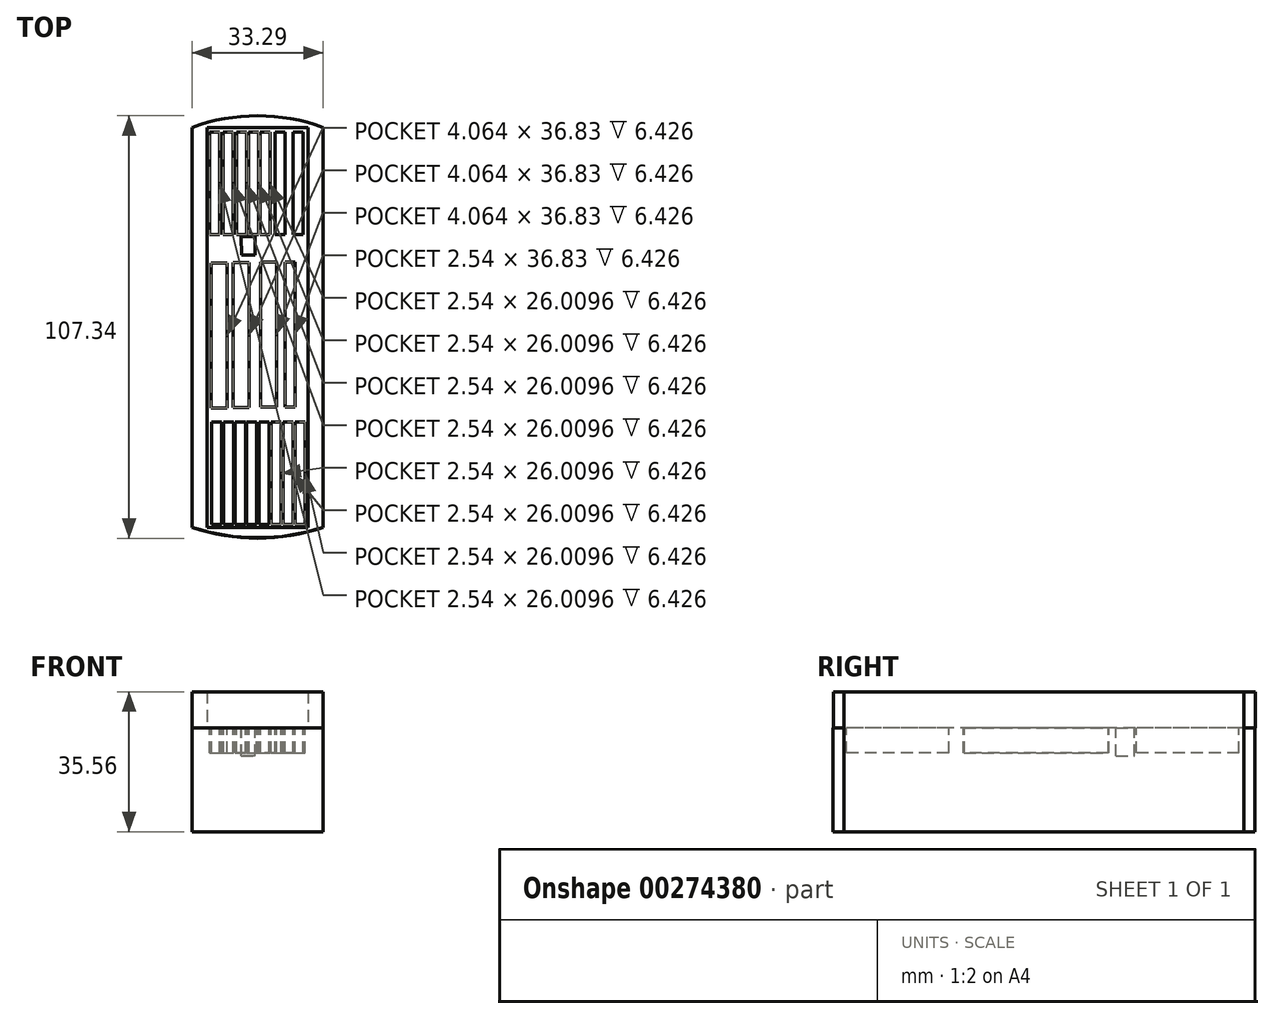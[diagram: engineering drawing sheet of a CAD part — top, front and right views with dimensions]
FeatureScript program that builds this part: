
annotation { "Feature Type Name" : "Feature", "Feature Type Description" : "" }
export const myFeature = defineFeature(function(context is Context, id is Id, definition is map)
    precondition{}
    {
        {
            var Q0;
            Q0=qCreatedBy(makeId("Top.planeOp"),FACE);
            var sketch = newSketch(context, id + "F0", { "sketchPlane" : qUnion([Q0])});
            skLineSegment(sketch, "E0", {"start": v(11.71, 60.5) * mm, "end": v(11.71, -41.1) * mm});
            skLineSegment(sketch, "E1", {"start": v(45, 60.5) * mm, "end": v(45, -41.1) * mm});
            skArc(sketch, "E2", {"start": v(45, 60.5) * mm, "mid": v(28.36, 63.3) * mm, "end": v(11.71, 60.5) * mm});
            skArc(sketch, "E3", {"start": v(11.71, -41.1) * mm, "mid": v(28.36, -43.9) * mm, "end": v(45, -41.1) * mm});
            skSolve(sketch);
        }
        {
            var Q0;
            Q0 = qSketchRegion(id + "F0", true);
            extrude(context, id + "F1", {"entities" : qUnion([Q0]), "depth" : 26.42 * mm});
        }
        {
            var Q0;
            Q0=makeQuery(id+"F1.opExtrude","CAP_FACE",FACE,{"disambiguationData":[OSD([sQuery(id+"F0.wireOp",EDGE,"E0"),sQuery(id+"F0.wireOp",EDGE,"E1"),sQuery(id+"F0.wireOp",EDGE,"E2"),sQuery(id+"F0.wireOp",EDGE,"E3")])],"isStart":false});
            var sketch = newSketch(context, id + "F2", { "sketchPlane" : qUnion([Q0])});
            skLineSegment(sketch, "E4", {"start": v(24.2, 32.75) * mm, "end": v(27.71, 32.75) * mm});
            skLineSegment(sketch, "E5", {"start": v(27.71, 32.75) * mm, "end": v(27.71, 28.02) * mm});
            skLineSegment(sketch, "E6", {"start": v(27.71, 28.02) * mm, "end": v(24.34, 28.02) * mm});
            skLineSegment(sketch, "E7", {"start": v(24.34, 28.02) * mm, "end": v(24.2, 32.75) * mm});
            skSolve(sketch);
        }
        {
            var Q0;
            Q0 = qSketchRegion(id + "F2", true);
            extrude(context, id + "F3", {"entities" : qUnion([Q0]), "operationType" : NewBodyOperationType.REMOVE, "oppositeDirection" : true, "depth" : 7.2 * mm});
        }
        {
            var Q0;
            Q0=makeQuery(id+"F1.opExtrude","CAP_FACE",FACE,{"disambiguationData":[OSD([sQuery(id+"F0.wireOp",EDGE,"E0"),sQuery(id+"F0.wireOp",EDGE,"E1"),sQuery(id+"F0.wireOp",EDGE,"E2"),sQuery(id+"F0.wireOp",EDGE,"E3")])],"isStart":false});
            var sketch = newSketch(context, id + "F4", { "sketchPlane" : qUnion([Q0])});
            skLineSegment(sketch, "E8", {"start": v(11.71, 60.5) * mm, "end": v(15.48, 60.5) * mm});
            skLineSegment(sketch, "E9", {"start": v(15.48, 60.5) * mm, "end": v(15.48, -41.1) * mm});
            skLineSegment(sketch, "E10", {"start": v(45, 60.5) * mm, "end": v(41.24, 60.5) * mm});
            skLineSegment(sketch, "E11", {"start": v(41.24, 60.5) * mm, "end": v(41.24, -41.1) * mm});
            skLineSegment(sketch, "E12", {"start": v(41.24, -41.1) * mm, "end": v(45, -41.1) * mm});
            skLineSegment(sketch, "E13", {"start": v(45, -41.1) * mm, "end": v(45, 60.5) * mm});
            skLineSegment(sketch, "E14", {"start": v(11.71, 60.5) * mm, "end": v(11.71, -41.1) * mm});
            skLineSegment(sketch, "E15", {"start": v(11.71, -41.1) * mm, "end": v(15.48, -41.1) * mm});
            skSolve(sketch);
        }
        {
            var Q0;
            Q0 = qSketchRegion(id + "F4", true);
            extrude(context, id + "F5", {"entities" : qUnion([Q0]), "operationType" : NewBodyOperationType.ADD, "depth" : 9.14 * mm});
        }
        {
            var Q0;
            Q0=makeQuery(id+"F1.opExtrude","CAP_FACE",FACE,{"disambiguationData":[OSD([sQuery(id+"F0.wireOp",EDGE,"E0"),sQuery(id+"F0.wireOp",EDGE,"E1"),sQuery(id+"F0.wireOp",EDGE,"E2"),sQuery(id+"F0.wireOp",EDGE,"E3")])],"isStart":false});
            var sketch = newSketch(context, id + "F6", { "sketchPlane" : qUnion([Q0])});
            skLineSegment(sketch, "E16.bottom", {"start": v(16.54, 26.06) * mm, "end": v(20.6, 26.06) * mm});
            skLineSegment(sketch, "E16.top", {"start": v(16.54, -10.77) * mm, "end": v(20.6, -10.77) * mm});
            skLineSegment(sketch, "E16.left", {"start": v(16.54, 26.06) * mm, "end": v(16.54, -10.77) * mm});
            skLineSegment(sketch, "E16.right", {"start": v(20.6, 26.06) * mm, "end": v(20.6, -10.77) * mm});
            skPoint(sketch, "E17.oppositeSnap0", {"position": v(30.78, -24.01) * mm});
            skLineSegment(sketch, "E18.bottom", {"start": v(26.22, -10.64) * mm, "end": v(22.15, -10.64) * mm});
            skLineSegment(sketch, "E18.top", {"start": v(26.22, 26.2) * mm, "end": v(22.15, 26.2) * mm});
            skLineSegment(sketch, "E18.left", {"start": v(26.22, -10.64) * mm, "end": v(26.22, 26.2) * mm});
            skLineSegment(sketch, "E18.right", {"start": v(22.15, -10.64) * mm, "end": v(22.15, 26.2) * mm});
            skLineSegment(sketch, "E19.bottom", {"start": v(33.2, -10.54) * mm, "end": v(29.14, -10.54) * mm});
            skLineSegment(sketch, "E19.top", {"start": v(33.2, 26.29) * mm, "end": v(29.14, 26.29) * mm});
            skLineSegment(sketch, "E19.left", {"start": v(33.2, -10.54) * mm, "end": v(33.2, 26.29) * mm});
            skLineSegment(sketch, "E19.right", {"start": v(29.14, -10.54) * mm, "end": v(29.14, 26.29) * mm});
            skLineSegment(sketch, "E20.bottom", {"start": v(37.85, -10.61) * mm, "end": v(35.3, -10.61) * mm});
            skLineSegment(sketch, "E20.top", {"start": v(37.85, 26.22) * mm, "end": v(35.3, 26.22) * mm});
            skLineSegment(sketch, "E20.left", {"start": v(37.85, -10.61) * mm, "end": v(37.85, 26.22) * mm});
            skLineSegment(sketch, "E20.right", {"start": v(35.3, -10.61) * mm, "end": v(35.3, 26.22) * mm});
            skLineSegment(sketch, "E21.bottom", {"start": v(16.67, -40.43) * mm, "end": v(19.21, -40.43) * mm});
            skLineSegment(sketch, "E21.top", {"start": v(16.67, -14.42) * mm, "end": v(19.21, -14.42) * mm});
            skLineSegment(sketch, "E21.left", {"start": v(16.67, -40.43) * mm, "end": v(16.67, -14.42) * mm});
            skLineSegment(sketch, "E21.right", {"start": v(19.21, -40.43) * mm, "end": v(19.21, -14.42) * mm});
            skLineSegment(sketch, "E22.bottom", {"start": v(19.69, -14.42) * mm, "end": v(22.23, -14.42) * mm});
            skLineSegment(sketch, "E22.top", {"start": v(19.69, -40.43) * mm, "end": v(22.23, -40.43) * mm});
            skLineSegment(sketch, "E22.left", {"start": v(19.69, -14.42) * mm, "end": v(19.69, -40.43) * mm});
            skLineSegment(sketch, "E22.right", {"start": v(22.23, -14.42) * mm, "end": v(22.23, -40.43) * mm});
            skLineSegment(sketch, "E23.bottom", {"start": v(22.71, -14.42) * mm, "end": v(25.25, -14.42) * mm});
            skLineSegment(sketch, "E23.top", {"start": v(22.71, -40.43) * mm, "end": v(25.25, -40.43) * mm});
            skLineSegment(sketch, "E23.left", {"start": v(22.71, -14.42) * mm, "end": v(22.71, -40.43) * mm});
            skLineSegment(sketch, "E23.right", {"start": v(25.25, -14.42) * mm, "end": v(25.25, -40.43) * mm});
            skLineSegment(sketch, "E24.bottom", {"start": v(25.6, -14.42) * mm, "end": v(28.14, -14.42) * mm});
            skLineSegment(sketch, "E24.top", {"start": v(25.6, -40.43) * mm, "end": v(28.14, -40.43) * mm});
            skLineSegment(sketch, "E24.left", {"start": v(25.6, -14.42) * mm, "end": v(25.6, -40.43) * mm});
            skLineSegment(sketch, "E24.right", {"start": v(28.14, -14.42) * mm, "end": v(28.14, -40.43) * mm});
            skLineSegment(sketch, "E25.bottom", {"start": v(28.79, -14.42) * mm, "end": v(31.33, -14.42) * mm});
            skLineSegment(sketch, "E25.top", {"start": v(28.79, -40.43) * mm, "end": v(31.33, -40.43) * mm});
            skLineSegment(sketch, "E25.left", {"start": v(28.79, -14.42) * mm, "end": v(28.79, -40.43) * mm});
            skLineSegment(sketch, "E25.right", {"start": v(31.33, -14.42) * mm, "end": v(31.33, -40.43) * mm});
            skLineSegment(sketch, "E26.bottom", {"start": v(31.82, -14.42) * mm, "end": v(34.36, -14.42) * mm});
            skLineSegment(sketch, "E26.top", {"start": v(31.82, -40.43) * mm, "end": v(34.36, -40.43) * mm});
            skLineSegment(sketch, "E26.left", {"start": v(31.82, -14.42) * mm, "end": v(31.82, -40.43) * mm});
            skLineSegment(sketch, "E26.right", {"start": v(34.36, -14.42) * mm, "end": v(34.36, -40.43) * mm});
            skLineSegment(sketch, "E27.bottom", {"start": v(34.87, -14.42) * mm, "end": v(37.41, -14.42) * mm});
            skLineSegment(sketch, "E27.top", {"start": v(34.87, -40.43) * mm, "end": v(37.41, -40.43) * mm});
            skLineSegment(sketch, "E27.left", {"start": v(34.87, -14.42) * mm, "end": v(34.87, -40.43) * mm});
            skLineSegment(sketch, "E27.right", {"start": v(37.41, -14.42) * mm, "end": v(37.41, -40.43) * mm});
            skPoint(sketch, "E28.firstSnap0", {"position": v(36.14, -14.42) * mm});
            skLineSegment(sketch, "E28.bottom", {"start": v(37.88, -14.42) * mm, "end": v(40.42, -14.42) * mm});
            skLineSegment(sketch, "E28.top", {"start": v(37.88, -40.43) * mm, "end": v(40.42, -40.43) * mm});
            skLineSegment(sketch, "E28.left", {"start": v(37.88, -14.42) * mm, "end": v(37.88, -40.43) * mm});
            skLineSegment(sketch, "E28.right", {"start": v(40.42, -14.42) * mm, "end": v(40.42, -40.43) * mm});
            skLineSegment(sketch, "E29.bottom", {"start": v(16.22, 59.28) * mm, "end": v(18.76, 59.28) * mm});
            skLineSegment(sketch, "E29.top", {"start": v(16.22, 33.27) * mm, "end": v(18.76, 33.27) * mm});
            skLineSegment(sketch, "E29.left", {"start": v(16.22, 59.28) * mm, "end": v(16.22, 33.27) * mm});
            skLineSegment(sketch, "E29.right", {"start": v(18.76, 59.28) * mm, "end": v(18.76, 33.27) * mm});
            skLineSegment(sketch, "E30.bottom", {"start": v(19.63, 59.28) * mm, "end": v(22.17, 59.28) * mm});
            skLineSegment(sketch, "E30.top", {"start": v(19.63, 33.27) * mm, "end": v(22.17, 33.27) * mm});
            skLineSegment(sketch, "E30.left", {"start": v(19.63, 59.28) * mm, "end": v(19.63, 33.27) * mm});
            skLineSegment(sketch, "E30.right", {"start": v(22.17, 59.28) * mm, "end": v(22.17, 33.27) * mm});
            skLineSegment(sketch, "E31.bottom", {"start": v(25.51, 59.28) * mm, "end": v(22.97, 59.28) * mm});
            skLineSegment(sketch, "E31.top", {"start": v(25.51, 33.27) * mm, "end": v(22.97, 33.27) * mm});
            skLineSegment(sketch, "E31.left", {"start": v(25.51, 59.28) * mm, "end": v(25.51, 33.27) * mm});
            skLineSegment(sketch, "E31.right", {"start": v(22.97, 59.28) * mm, "end": v(22.97, 33.27) * mm});
            skLineSegment(sketch, "E32.bottom", {"start": v(26.1, 59.28) * mm, "end": v(28.64, 59.28) * mm});
            skLineSegment(sketch, "E32.top", {"start": v(26.1, 33.27) * mm, "end": v(28.64, 33.27) * mm});
            skLineSegment(sketch, "E32.left", {"start": v(26.1, 59.28) * mm, "end": v(26.1, 33.27) * mm});
            skLineSegment(sketch, "E32.right", {"start": v(28.64, 59.28) * mm, "end": v(28.64, 33.27) * mm});
            skLineSegment(sketch, "E33.bottom", {"start": v(29, 59.28) * mm, "end": v(31.53, 59.28) * mm});
            skLineSegment(sketch, "E33.top", {"start": v(29, 33.27) * mm, "end": v(31.53, 33.27) * mm});
            skLineSegment(sketch, "E33.left", {"start": v(29, 59.28) * mm, "end": v(29, 33.27) * mm});
            skLineSegment(sketch, "E33.right", {"start": v(31.53, 59.28) * mm, "end": v(31.53, 33.27) * mm});
            skLineSegment(sketch, "E34.bottom", {"start": v(32.8, 59.28) * mm, "end": v(35.34, 59.28) * mm});
            skLineSegment(sketch, "E34.top", {"start": v(32.8, 33.27) * mm, "end": v(35.34, 33.27) * mm});
            skLineSegment(sketch, "E34.left", {"start": v(32.8, 59.28) * mm, "end": v(32.8, 33.27) * mm});
            skLineSegment(sketch, "E34.right", {"start": v(35.34, 59.28) * mm, "end": v(35.34, 33.27) * mm});
            skLineSegment(sketch, "E35.bottom", {"start": v(37.4, 59.28) * mm, "end": v(39.93, 59.28) * mm});
            skLineSegment(sketch, "E35.top", {"start": v(37.4, 33.27) * mm, "end": v(39.93, 33.27) * mm});
            skLineSegment(sketch, "E35.left", {"start": v(37.4, 59.28) * mm, "end": v(37.4, 33.27) * mm});
            skLineSegment(sketch, "E35.right", {"start": v(39.93, 59.28) * mm, "end": v(39.93, 33.27) * mm});
            skSolve(sketch);
        }
        {
            var Q0;
            Q0 = qSketchRegion(id + "F6", true);
            extrude(context, id + "F7", {"entities" : qUnion([Q0]), "operationType" : NewBodyOperationType.REMOVE, "oppositeDirection" : true, "depth" : 6.43 * mm});
        }
        {
            var Q0;
            Q0=makeQuery(id+"F1.opExtrude","CAP_FACE",FACE,{"disambiguationData":[OSD([sQuery(id+"F0.wireOp",EDGE,"E0"),sQuery(id+"F0.wireOp",EDGE,"E1"),sQuery(id+"F0.wireOp",EDGE,"E2"),sQuery(id+"F0.wireOp",EDGE,"E3")])],"isStart":false});
            var sketch = newSketch(context, id + "F8", { "sketchPlane" : qUnion([Q0])});
            skArc(sketch, "E36", {"start": v(45, 60.5) * mm, "mid": v(28.36, 63.44) * mm, "end": v(11.71, 60.5) * mm});
            skLineSegment(sketch, "E37", {"start": v(11.71, 60.5) * mm, "end": v(45, 60.5) * mm});
            skArc(sketch, "E38", {"start": v(11.71, -41.1) * mm, "mid": v(28.36, -43.76) * mm, "end": v(45, -41.1) * mm});
            skLineSegment(sketch, "E39", {"start": v(11.71, -41.1) * mm, "end": v(45, -41.1) * mm});
            skSolve(sketch);
        }
        {
            var Q0;
            Q0 = qSketchRegion(id + "F8", true);
            extrude(context, id + "F9", {"entities" : qUnion([Q0]), "operationType" : NewBodyOperationType.ADD, "depth" : 9.14 * mm});
        }
    });
